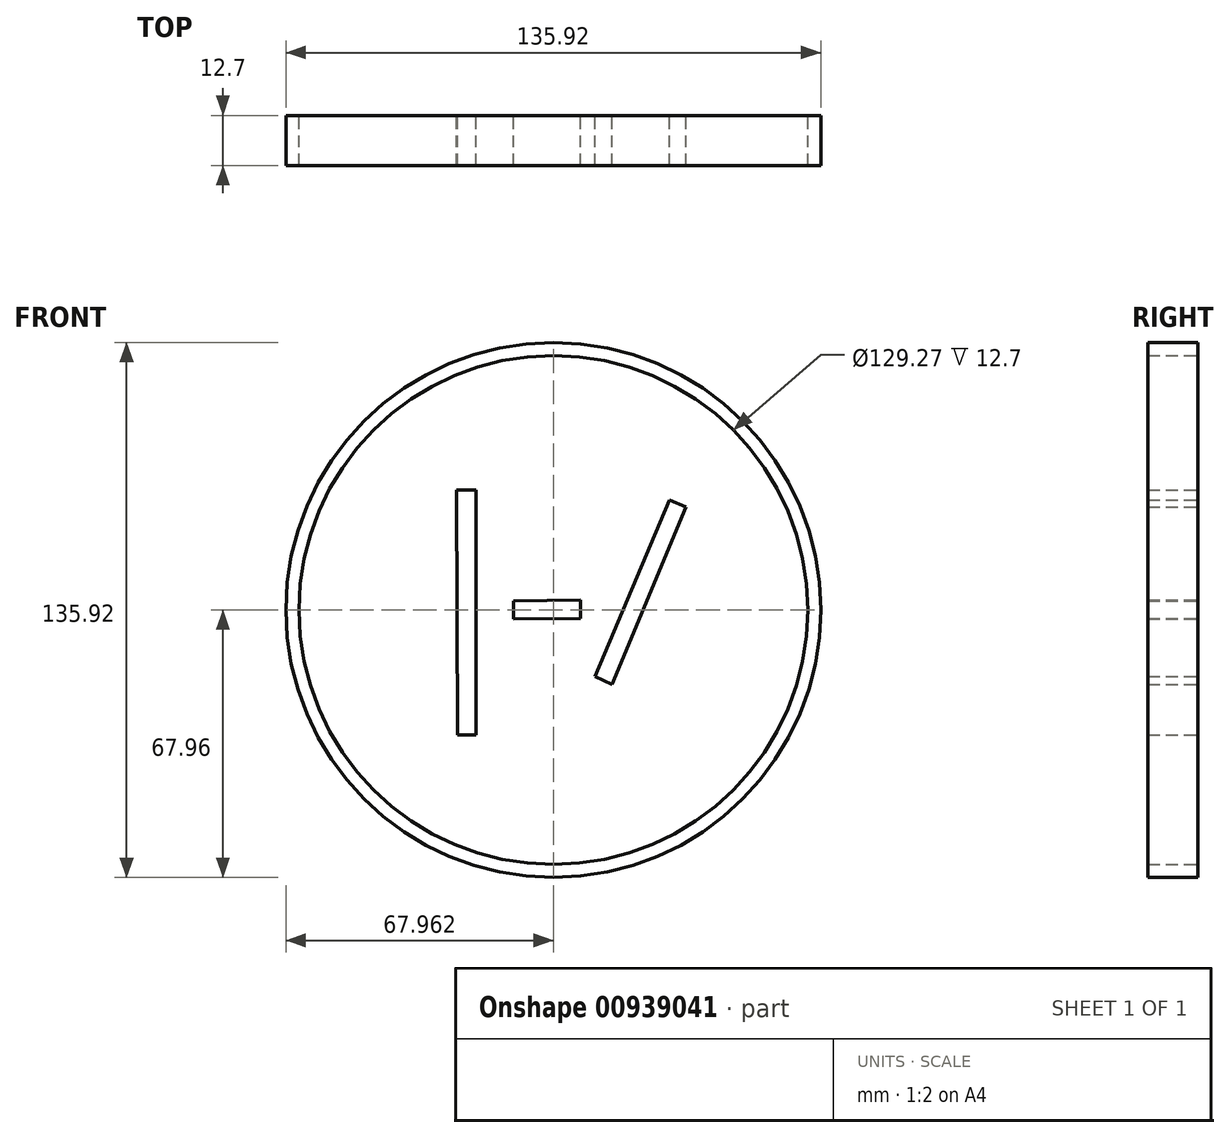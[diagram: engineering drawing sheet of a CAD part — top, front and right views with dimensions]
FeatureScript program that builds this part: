
annotation { "Feature Type Name" : "Feature", "Feature Type Description" : "" }
export const myFeature = defineFeature(function(context is Context, id is Id, definition is map)
    precondition{}
    {
        {
            var Q0;
            Q0=qCreatedBy(makeId("Front.planeOp"),FACE);
            var sketch = newSketch(context, id + "F0", { "sketchPlane" : qUnion([Q0])});
            skLineSegment(sketch, "E0", {"start": v(-22.82, 30.48) * mm, "end": v(-17.82, 30.48) * mm});
            skLineSegment(sketch, "E1", {"start": v(-17.82, 30.48) * mm, "end": v(-17.82, -31.79) * mm});
            skLineSegment(sketch, "E2", {"start": v(-17.82, -31.79) * mm, "end": v(-22.52, -31.79) * mm});
            skLineSegment(sketch, "E3", {"start": v(-22.52, -31.79) * mm, "end": v(-22.82, 30.48) * mm});
            skLineSegment(sketch, "E4", {"start": v(-8.35, 2.33) * mm, "end": v(-8.35, -2.3) * mm});
            skLineSegment(sketch, "E5", {"start": v(8.76, -2.13) * mm, "end": v(8.76, 2.49) * mm});
            skLineSegment(sketch, "E6", {"start": v(8.76, 2.49) * mm, "end": v(-8.35, 2.33) * mm});
            skLineSegment(sketch, "E7", {"start": v(12.4, -16.92) * mm, "end": v(16.7, -18.9) * mm});
            skLineSegment(sketch, "E8", {"start": v(16.7, -18.9) * mm, "end": v(35.5, 26.18) * mm});
            skLineSegment(sketch, "E9", {"start": v(35.5, 26.18) * mm, "end": v(31.34, 27.9) * mm});
            skLineSegment(sketch, "E10", {"start": v(31.34, 27.9) * mm, "end": v(12.4, -16.92) * mm});
            skCircle(sketch, "E11", {"center": v(1.81, 0) * mm, "radius": 64.64 * mm});
            skLineSegment(sketch, "E12", {"start": v(-8.35, -2.3) * mm, "end": v(8.76, -2.13) * mm});
            skCircle(sketch, "E13", {"center": v(1.81, 0) * mm, "radius": 67.96 * mm});
            skSolve(sketch);
        }
        {
            var Q0;
            Q0 = qSketchRegion(id + "F0", true);
            var Q1;
            Q1=makeQuery(id+"F0.imprint","IMPRINT",FACE,{"disambiguationData":[TD([[makeQuery(id+"F0.imprint","IMPRINT",EDGE,{"derivedFrom":sQuery(id+"F0.wireOp",EDGE,"E7")}),1.0]])]});
            var Q2;
            Q2=makeQuery(id+"F0.imprint","IMPRINT",FACE,{"disambiguationData":[TD([[makeQuery(id+"F0.imprint","IMPRINT",EDGE,{"derivedFrom":sQuery(id+"F0.wireOp",EDGE,"E4")}),1.0]])]});
            var Q3;
            Q3=makeQuery(id+"F0.imprint","IMPRINT",FACE,{"disambiguationData":[TD([[makeQuery(id+"F0.imprint","IMPRINT",EDGE,{"derivedFrom":sQuery(id+"F0.wireOp",EDGE,"E0")}),-1.0]])]});
            extrude(context, id + "F1", {"entities" : qUnion([Q0, Q1, Q2, Q3]), "depth" : 12.7 * mm, "offsetDistance" : 25.4 * mm});
        }
    });
